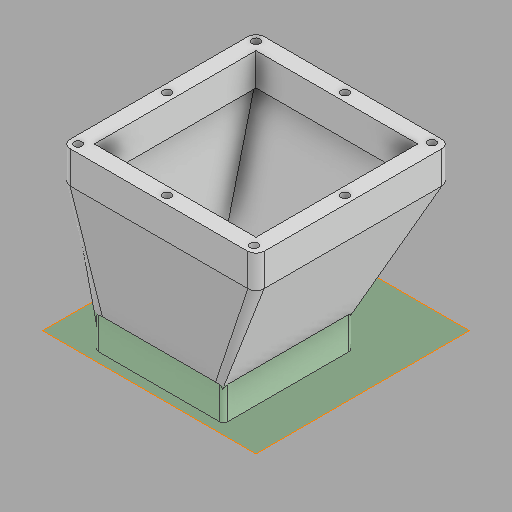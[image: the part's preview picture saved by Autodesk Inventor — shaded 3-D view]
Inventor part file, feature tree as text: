
AUTODESK INVENTOR PART (.ipt)
format: ipt  version: 2025 (Build 290162000, 162)  size: 447,488 bytes
history: native  units: in
note: dims shown in document units (in); Inventor stores cm internally (conversion verified against a paired STEP export)
features: sketch x6, extrude x3, fillet x2, plane x1, loft x1, shell x1, hole x1, other x1
ambient origin geometry x8: Origin, YZ Plane, XZ Plane, XY Plane, X Axis, Y Axis, Z Axis, Center Point
bodies: Solid1 (feature_tree)
feature tree (16):
  extrude  "Extrusion1"  Depth=6.0in
  fillet  "Fillet1"  Radius=5.0in
  plane  "Work Plane1"
  loft  "Loft1"
  sketch  "Sketch3"  dims[d8=2.0in d9=4.0in]
  shell  "Shell3"  Thickness=4.0in
  extrude  "Extrusion2"  Depth=4.0in
  hole  "Hole1"  [1 undecoded]
  extrude  "Extrusion4"  Depth=1.0in TaperAngle=0.0deg
  fillet  "Fillet3"  Radius=0.25in
  sketch  "Sketch1"  dims[d0=6.0in d1=6.0in d2=5.0in]
  sketch  "Sketch2"  dims[d3=1.0in d4=0.0in d5=0.25in d6=4.0in]
  other  "Edges1"
  sketch  "Sketch4"  dims[d10=4.0in d13=0.0in d14=90.0deg]
  sketch  "Sketch7"  dims[d15=0.0in d16=90.0deg d19=1.0in d20=0.0in d27=0.25in]
  sketch  "Sketch8"  dims[d28=2.4in d29=1.0in d30=3.1969in d31=0.75in d32=0.375in d33=0.25in d34=0.5635in d35=5.0in d36=0.0in d38=0.25in d39=0.25in d40=0.25in d41=0.5in d42=0.0in d43=0.125in d37=0.0625in d44=1.0in d45=1.0in d46=0.15in d47=0.25in d48=0.375in d49=0.5635in d50=0.75in d51=0.8108in d52=0.0625in d53=0.75in d54=0.375in]
note: 1 required parameter value undecoded (feature->parameter linkage not recoverable at this tier; creation-order binding heuristic only, values carry confidence <= 0.55)
